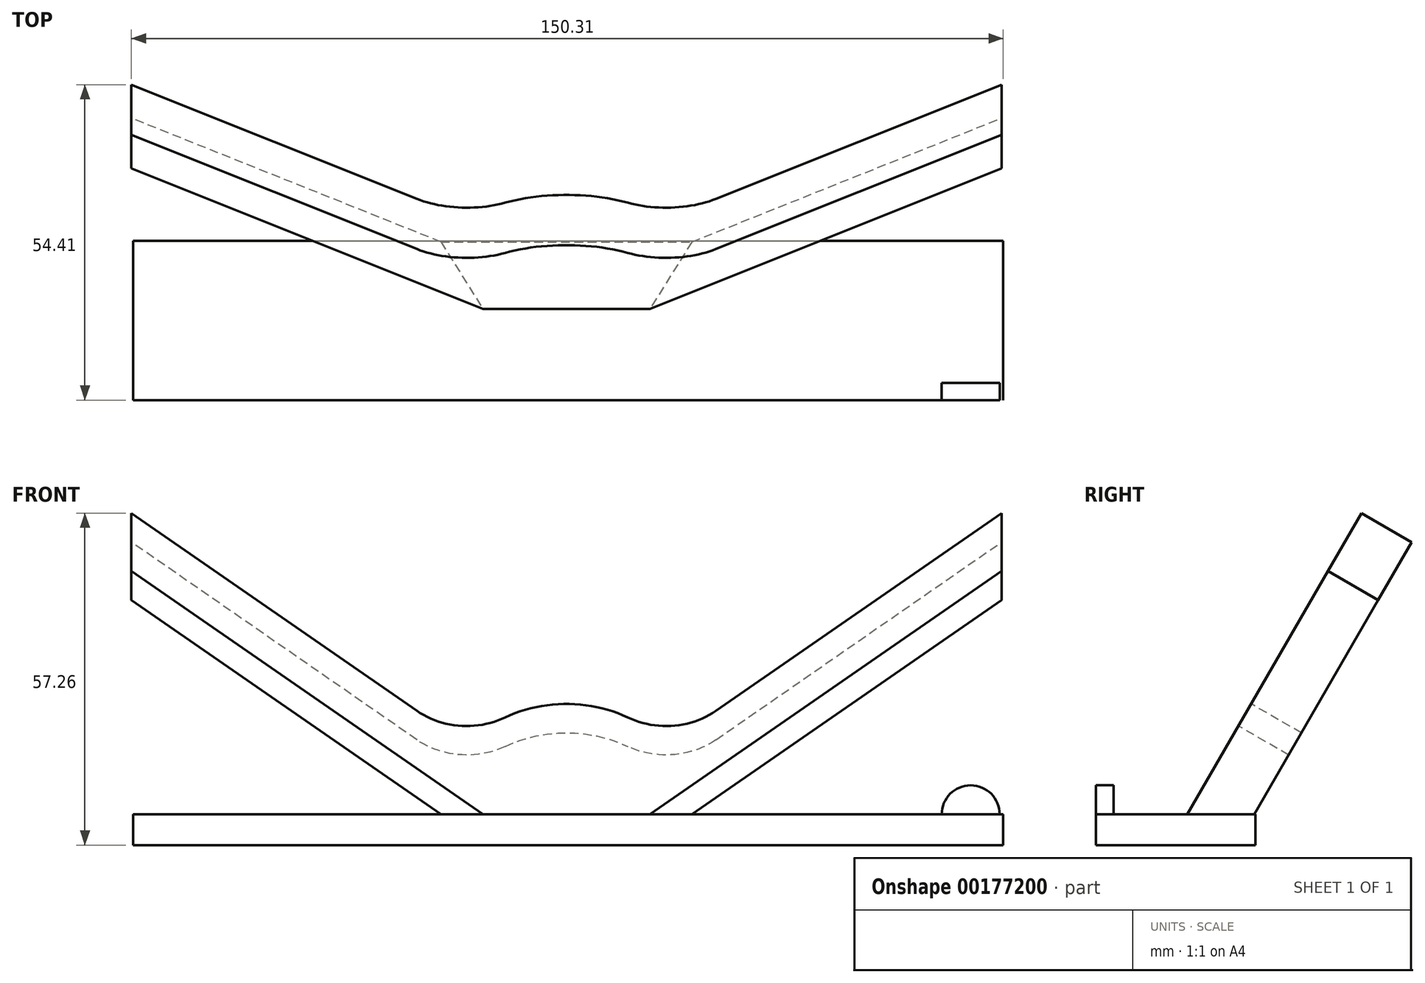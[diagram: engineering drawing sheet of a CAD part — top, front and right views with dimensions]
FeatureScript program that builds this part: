
annotation { "Feature Type Name" : "Feature", "Feature Type Description" : "" }
export const myFeature = defineFeature(function(context is Context, id is Id, definition is map)
    precondition{}
    {
        {
            var Q0;
            Q0=qCreatedBy(makeId("Right.planeOp"),FACE);
            var sketch = newSketch(context, id + "F0", { "sketchPlane" : qUnion([Q0])});
            skLineSegment(sketch, "E0", {"start": v(0, 0) * mm, "end": v(31.73, 54.96) * mm, "construction": true});
            skSolve(sketch);
        }
        {
            var Q0;
            Q0=qCreatedBy(makeId("Front.planeOp"),FACE);
            var Q1;
            Q1=sQuery(id+"F0.wireOp",EDGE,"E0");
            cPlane(context, id + "F1", {"entities" : qUnion([Q0, Q1]), "cplaneType" : CPlaneType.LINE_ANGLE, "offset" : 25 * mm, "angle" : 0 * degree, "width" : 150 * mm, "height" : 150 * mm});
        }
        {
            var Q0;
            Q0=qCreatedBy(id+"F1.planeOp",FACE);
            var sketch = newSketch(context, id + "F2", { "sketchPlane" : qUnion([Q0])});
            skLineSegment(sketch, "E1", {"start": v(0, 0) * mm, "end": v(-75, 0) * mm, "construction": true});
            skLineSegment(sketch, "E2", {"start": v(-75, 0) * mm, "end": v(-75, 60) * mm, "construction": true});
            skLineSegment(sketch, "E3", {"start": v(-25.77, 20.61) * mm, "end": v(-75, 60) * mm});
            skLineSegment(sketch, "E4", {"start": v(-14.4, 0) * mm, "end": v(-75, 48.47) * mm});
            skLineSegment(sketch, "E5", {"start": v(-75, 60) * mm, "end": v(-75, 48.47) * mm});
            skLineSegment(sketch, "E6", {"start": v(0, 0) * mm, "end": v(-14.4, 0) * mm});
            skLineSegment(sketch, "E7.MirrorCS", {"start": v(14.4, 0) * mm, "end": v(75, 48.47) * mm});
            skLineSegment(sketch, "E8.MirrorCS", {"start": v(75, 60) * mm, "end": v(75, 48.47) * mm});
            skLineSegment(sketch, "E9.MirrorCS", {"start": v(0, 0) * mm, "end": v(14.4, 0) * mm});
            skArc(sketch, "E10", {"start": v(10.57, 19.3) * mm, "mid": v(0, 22) * mm, "end": v(-10.57, 19.3) * mm});
            skArc(sketch, "E11", {"start": v(-25.77, 20.61) * mm, "mid": v(-18.37, 17.65) * mm, "end": v(-10.57, 19.3) * mm});
            skArc(sketch, "E12.MirrorCS", {"start": v(25.77, 20.61) * mm, "mid": v(18.37, 17.65) * mm, "end": v(10.57, 19.3) * mm});
            skLineSegment(sketch, "E13.trimOffspring", {"start": v(25.77, 20.61) * mm, "end": v(75, 60) * mm});
            skPoint(sketch, "E14.orphan", {"position": v(-17.18, 13.74) * mm});
            skSolve(sketch);
        }
        {
            var Q0;
            Q0=makeQuery(id+"F2.imprint","IMPRINT",FACE,{"disambiguationData":[TD([[makeQuery(id+"F2.imprint","IMPRINT",EDGE,{"derivedFrom":sQuery(id+"F2.wireOp",EDGE,"E3")}),1.0]])]});
            extrude(context, id + "F3", {"entities" : qUnion([Q0]), "depth" : 10 * mm, "offsetDistance" : 25 * mm});
        }
        {
            var Q0;
            Q0=qCreatedBy(makeId("Front.planeOp"),FACE);
            var sketch = newSketch(context, id + "F4", { "sketchPlane" : qUnion([Q0])});
            skLineSegment(sketch, "E15.bottom", {"start": v(-74.7, 0) * mm, "end": v(75.3, 0) * mm});
            skLineSegment(sketch, "E15.top", {"start": v(-74.7, -5.3) * mm, "end": v(75.3, -5.3) * mm});
            skLineSegment(sketch, "E15.left", {"start": v(-74.7, 0) * mm, "end": v(-74.7, -5.3) * mm});
            skLineSegment(sketch, "E15.right", {"start": v(75.3, 0) * mm, "end": v(75.3, -5.3) * mm});
            skSolve(sketch);
        }
        {
            var Q0;
            Q0=makeQuery(id+"F4.imprint","IMPRINT",FACE,{"disambiguationData":[TD([[makeQuery(id+"F4.imprint","IMPRINT",EDGE,{"derivedFrom":sQuery(id+"F4.wireOp",EDGE,"E15.bottom")}),-1.0]])]});
            extrude(context, id + "F5", {"entities" : qUnion([Q0]), "operationType" : NewBodyOperationType.ADD, "endBound" : BoundingType.SYMMETRIC, "depth" : 23.5 * mm, "offsetDistance" : 25 * mm});
        }
        {
            var Q0;
            Q0=makeQuery(id+"F5.opExtrude","CAP_FACE",FACE,{"disambiguationData":[OSD([sQuery(id+"F4.wireOp",EDGE,"E15.bottom"),sQuery(id+"F4.wireOp",EDGE,"E15.top"),sQuery(id+"F4.wireOp",EDGE,"E15.left"),sQuery(id+"F4.wireOp",EDGE,"E15.right")])],"isStart":false});
            var sketch = newSketch(context, id + "F6", { "sketchPlane" : qUnion([Q0])});
            skLineSegment(sketch, "E16.bottom", {"start": v(-74.7, -5.3) * mm, "end": v(75.3, -5.3) * mm});
            skLineSegment(sketch, "E16.top", {"start": v(-74.7, 0) * mm, "end": v(75.3, 0) * mm});
            skLineSegment(sketch, "E16.left", {"start": v(-74.7, -5.3) * mm, "end": v(-74.7, 0) * mm});
            skLineSegment(sketch, "E16.right", {"start": v(75.3, -5.3) * mm, "end": v(75.3, 0) * mm});
            skSolve(sketch);
        }
        {
            var Q0;
            Q0 = qSketchRegion(id + "F6", true);
            extrude(context, id + "F7", {"entities" : qUnion([Q0]), "operationType" : NewBodyOperationType.ADD, "depth" : 4 * mm, "offsetDistance" : 25 * mm});
        }
        {
            var Q0;
            Q0=makeQuery(id+"F7.opExtrude","CAP_FACE",FACE,{"disambiguationData":[OSD([sQuery(id+"F6.wireOp",EDGE,"E16.bottom"),sQuery(id+"F6.wireOp",EDGE,"E16.top"),sQuery(id+"F6.wireOp",EDGE,"E16.left"),sQuery(id+"F6.wireOp",EDGE,"E16.right")])],"isStart":false});
            var sketch = newSketch(context, id + "F8", { "sketchPlane" : qUnion([Q0])});
            skArc(sketch, "E17", {"start": v(-74.7, 0) * mm, "mid": v(-69.7, 5) * mm, "end": v(-64.7, 0) * mm});
            skArc(sketch, "E18.MirrorCS", {"start": v(74.7, 0) * mm, "mid": v(69.7, 5) * mm, "end": v(64.7, 0) * mm});
            skSolve(sketch);
        }
        {
            var Q0;
            {var subQ0=sQuery(id+"F8.wireOp",EDGE,"E17");Q0=makeQuery(id+"F8.imprint","IMPRINT",FACE,{"disambiguationData":[TD([[makeQuery(id+"F8.imprint","IMPRINT",EDGE,{"derivedFrom":subQ0}),-1.0]])]});}
            var Q1;
            {var subQ0=sQuery(id+"F8.wireOp",EDGE,"E18.MirrorCS");Q1=makeQuery(id+"F8.imprint","IMPRINT",FACE,{"disambiguationData":[TD([[makeQuery(id+"F8.imprint","IMPRINT",EDGE,{"derivedFrom":subQ0}),1.0]])]});}
            extrude(context, id + "F9", {"entities" : qUnion([Q0, Q1]), "oppositeDirection" : true, "depth" : 3 * mm, "offsetDistance" : 25 * mm});
        }
    });
